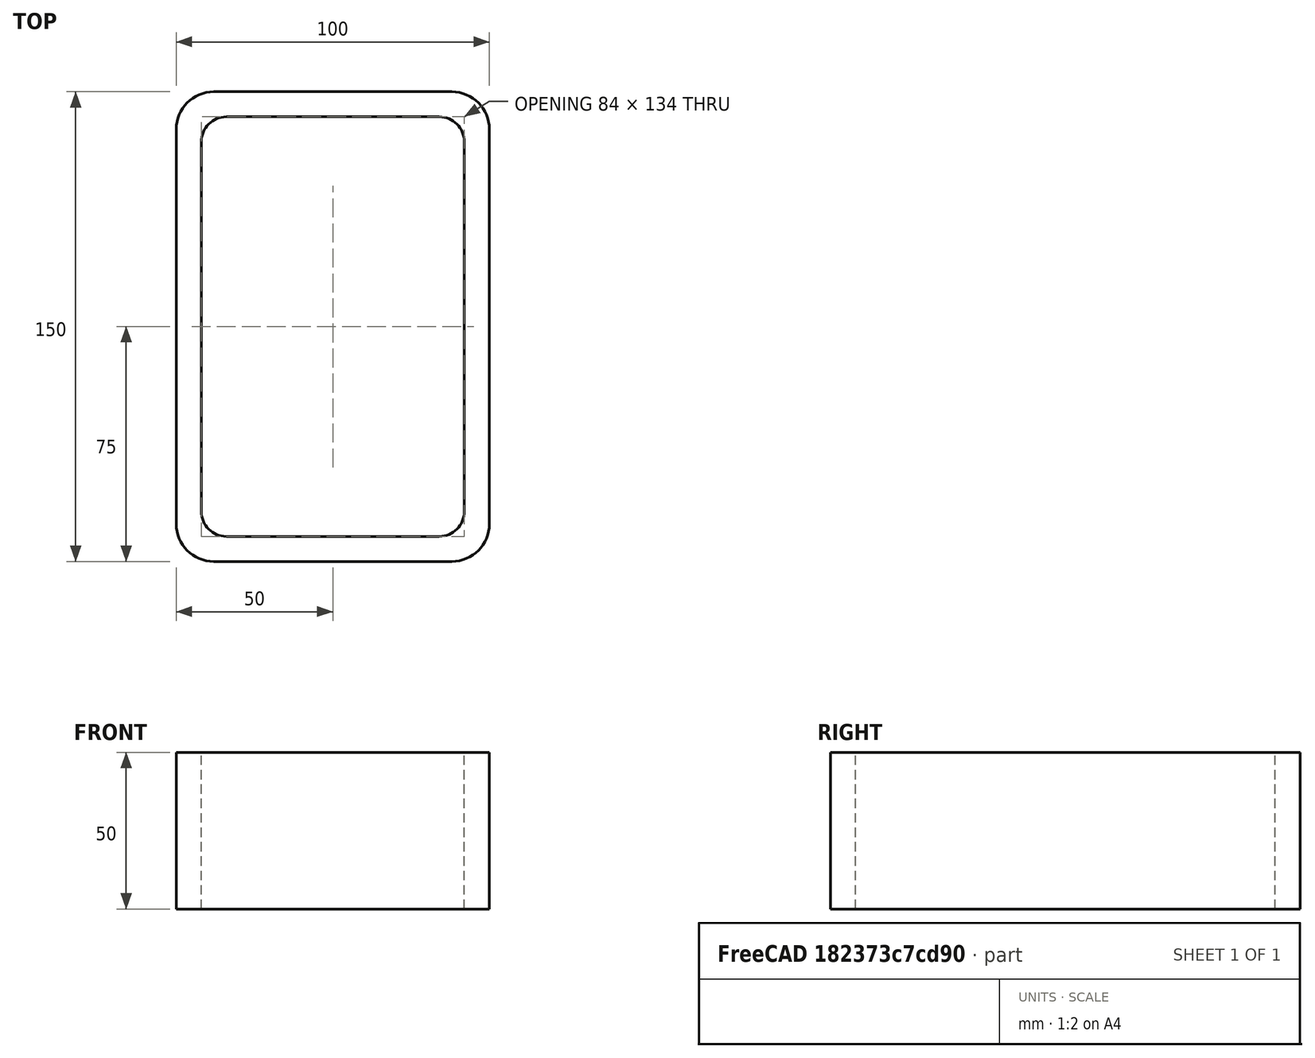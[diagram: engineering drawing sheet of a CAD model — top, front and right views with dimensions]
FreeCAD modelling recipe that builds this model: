
FCSTD DOCUMENT  (FreeCAD 0.15R4671 (Git))
Label: Rectangular hollow section 150x100x8 EN10219 S235JRH
License: All rights reserved
LicenseURL: http://en.wikipedia.org/wiki/All_rights_reserved
objects: Sketcher::SketchObject×1, Part::Extrusion×1
note: 2 computed .brp shape members not serialized (recipe doc carries the construction recipe); baked Part::Feature solids carry a one-line shape summary decoded from their .brp

FEATURE [Sketcher::SketchObject] Sketch
  sketch-geometry (16):
    g0: LineSegment StartX=-34 StartY=67 StartZ=0 EndX=34 EndY=67 EndZ=0
    g1: LineSegment StartX=42 StartY=59 StartZ=0 EndX=42 EndY=-59 EndZ=0
    g2: LineSegment StartX=34 StartY=-67 StartZ=0 EndX=-34 EndY=-67 EndZ=0
    g3: LineSegment StartX=-42 StartY=-59 StartZ=0 EndX=-42 EndY=59 EndZ=0
    g4: LineSegment StartX=-38 StartY=75 StartZ=0 EndX=38 EndY=75 EndZ=0
    g5: LineSegment StartX=50 StartY=63 StartZ=0 EndX=50 EndY=-63 EndZ=0
    g6: LineSegment StartX=38 StartY=-75 StartZ=0 EndX=-38 EndY=-75 EndZ=0
    g7: LineSegment StartX=-50 StartY=-63 StartZ=0 EndX=-50 EndY=63 EndZ=0
    g8: ArcOfCircle CenterX=-34 CenterY=59 CenterZ=0 NormalX=0 NormalY=0 NormalZ=1 Radius=8 StartAngle=1.5708 EndAngle=3.14159
    g9: ArcOfCircle CenterX=34 CenterY=59 CenterZ=0 NormalX=0 NormalY=0 NormalZ=1 Radius=8 StartAngle=0 EndAngle=1.5708
    g10: ArcOfCircle CenterX=34 CenterY=-59 CenterZ=0 NormalX=0 NormalY=0 NormalZ=1 Radius=8 StartAngle=4.71239 EndAngle=6.28319
    g11: ArcOfCircle CenterX=-34 CenterY=-59 CenterZ=0 NormalX=0 NormalY=0 NormalZ=1 Radius=8 StartAngle=3.14159 EndAngle=4.71239
    g12: ArcOfCircle CenterX=38 CenterY=63 CenterZ=0 NormalX=0 NormalY=0 NormalZ=1 Radius=12 StartAngle=0 EndAngle=1.5708
    g13: ArcOfCircle CenterX=38 CenterY=-63 CenterZ=0 NormalX=0 NormalY=0 NormalZ=1 Radius=12 StartAngle=4.71239 EndAngle=6.28319
    g14: ArcOfCircle CenterX=-38 CenterY=-63 CenterZ=0 NormalX=0 NormalY=0 NormalZ=1 Radius=12 StartAngle=3.14159 EndAngle=4.71239
    g15: ArcOfCircle CenterX=-38 CenterY=63 CenterZ=0 NormalX=0 NormalY=0 NormalZ=1 Radius=12 StartAngle=1.5708 EndAngle=3.14159
  constraints (36):
    c: Horizontal(g2)
    c: Vertical(g3)
    c: Horizontal(g6)
    c: Vertical(g7)
    c: Tangent(g3,g8) = 1.5708
    c: Tangent(g0,g8) = 1.5708
    c: Tangent(g0,g9) = 1.5708
    c: Tangent(g1,g9) = 1.5708
    c: Tangent(g1,g10) = 1.5708
    c: Tangent(g2,g10) = 1.5708
    c: Tangent(g2,g11) = 1.5708
    c: Tangent(g3,g11) = 1.5708
    c: Tangent(g4,g12) = 1.5708
    c: Tangent(g5,g12) = 1.5708
    c: Tangent(g5,g13) = 1.5708
    c: Tangent(g6,g13) = 1.5708
    c: Tangent(g6,g14) = 1.5708
    c: Tangent(g7,g14) = 1.5708
    c: Tangent(g7,g15) = 1.5708
    c: Tangent(g4,g15) = 1.5708
    c: Equal(g9,g8)
    c: Equal(g9,g11)
    c: Equal(g9,g10)
    c: Equal(g12,g15)
    c: Equal(g12,g14)
    c: Equal(g12,g13)
    c: Symmetric(g4,g6,g-1)
    c: Symmetric(g7,g5,g-2)
    c: DistanceY(g4,g6) = -150
    c: DistanceX(g7,g5) = 100
    c: Symmetric(g3,g1,g-2)
    c: Symmetric(g0,g2,g-1)
    c: DistanceY(g0,g4) = 8
    c: DistanceX(g5,g1) = -8
    c: Radius(g9) = 8
    c: Radius(g12) = 12
FEATURE [Part::Extrusion] Extrude  label="Rectangular hollow section 150x100x8 EN10219 S235JRH"
  Base = -> Sketch
  Dir = (0,0,50)
  Solid = true
